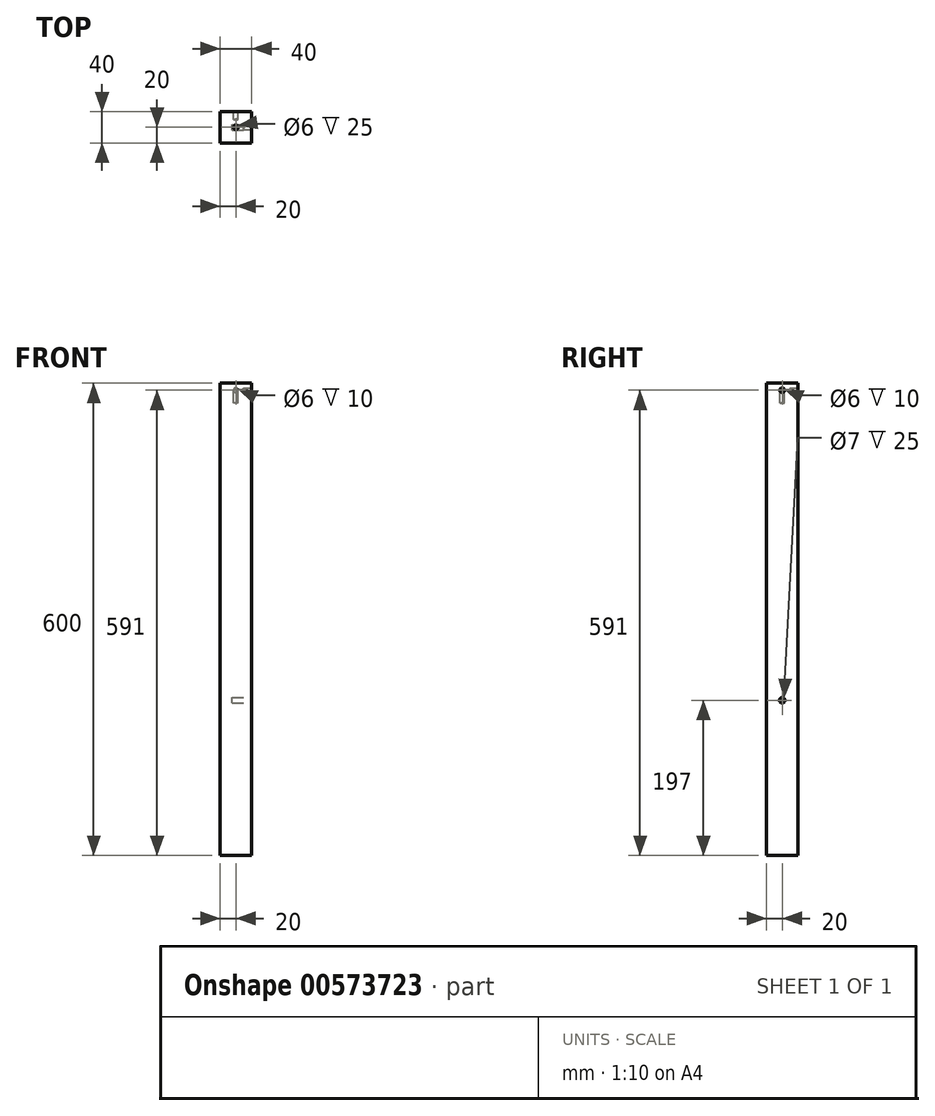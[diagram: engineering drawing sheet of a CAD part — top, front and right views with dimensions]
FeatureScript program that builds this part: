
annotation { "Feature Type Name" : "Feature", "Feature Type Description" : "" }
export const myFeature = defineFeature(function(context is Context, id is Id, definition is map)
    precondition{}
    {
        {
            var Q0;
            Q0=qCreatedBy(makeId("Top.planeOp"),FACE);
            var sketch = newSketch(context, id + "F0", { "sketchPlane" : qUnion([Q0])});
            skLineSegment(sketch, "E0.bottom", {"start": v(0, 0) * mm, "end": v(40, 0) * mm});
            skLineSegment(sketch, "E0.top", {"start": v(0, 40) * mm, "end": v(40, 40) * mm});
            skLineSegment(sketch, "E0.left", {"start": v(0, 0) * mm, "end": v(0, 40) * mm});
            skLineSegment(sketch, "E0.right", {"start": v(40, 0) * mm, "end": v(40, 40) * mm});
            skSolve(sketch);
        }
        {
            var Q0;
            Q0=makeQuery(id+"F0.imprint","IMPRINT",FACE,{"disambiguationData":[TD([[makeQuery(id+"F0.imprint","IMPRINT",EDGE,{"derivedFrom":sQuery(id+"F0.wireOp",EDGE,"E0.bottom")}),1.0]])]});
            extrude(context, id + "F1", {"entities" : qUnion([Q0]), "depth" : 600 * mm, "offsetDistance" : 25 * mm});
        }
        {
            var Q0;
            Q0=makeQuery(id+"F1.opExtrude","CAP_FACE",FACE,{"disambiguationData":[OSD([sQuery(id+"F0.wireOp",EDGE,"E0.bottom"),sQuery(id+"F0.wireOp",EDGE,"E0.top"),sQuery(id+"F0.wireOp",EDGE,"E0.left"),sQuery(id+"F0.wireOp",EDGE,"E0.right")])],"isStart":false});
            var sketch = newSketch(context, id + "F2", { "sketchPlane" : qUnion([Q0])});
            skCircle(sketch, "E1", {"center": v(20, 20) * mm, "radius": 3 * mm});
            skPoint(sketch, "E2", {"position": v(20, 40) * mm});
            skPoint(sketch, "E3", {"position": v(0, 20) * mm});
            skSolve(sketch);
        }
        {
            var Q0;
            Q0 = qSketchRegion(id + "F2", true);
            extrude(context, id + "F3", {"entities" : qUnion([Q0]), "operationType" : NewBodyOperationType.REMOVE, "oppositeDirection" : true, "depth" : 25 * mm, "offsetDistance" : 25 * mm});
        }
        {
            var Q0;
            Q0=makeQuery(id+"F1.opExtrude","SWEPT_FACE",FACE,{"disambiguationData":[OSD([sQuery(id+"F0.wireOp",EDGE,"E0.right")])]});
            var sketch = newSketch(context, id + "F4", { "sketchPlane" : qUnion([Q0])});
            skCircle(sketch, "E4", {"center": v(20, 591) * mm, "radius": 3 * mm});
            skPoint(sketch, "E5", {"position": v(20, 600) * mm});
            skSolve(sketch);
        }
        {
            var Q0;
            Q0 = qSketchRegion(id + "F4", true);
            extrude(context, id + "F5", {"entities" : qUnion([Q0]), "operationType" : NewBodyOperationType.REMOVE, "oppositeDirection" : true, "depth" : 10 * mm, "offsetDistance" : 25 * mm});
        }
        {
            var Q0;
            Q0=makeQuery(id+"F1.opExtrude","SWEPT_FACE",FACE,{"disambiguationData":[OSD([sQuery(id+"F0.wireOp",EDGE,"E0.top")])]});
            var sketch = newSketch(context, id + "F6", { "sketchPlane" : qUnion([Q0])});
            skCircle(sketch, "E6", {"center": v(-20, 591) * mm, "radius": 3 * mm});
            skPoint(sketch, "E7", {"position": v(-20, 600) * mm});
            skSolve(sketch);
        }
        {
            var Q0;
            Q0 = qSketchRegion(id + "F6", true);
            extrude(context, id + "F7", {"entities" : qUnion([Q0]), "operationType" : NewBodyOperationType.REMOVE, "oppositeDirection" : true, "depth" : 10 * mm, "offsetDistance" : 25 * mm});
        }
        {
            var Q0;
            Q0=makeQuery(id+"F1.opExtrude","SWEPT_FACE",FACE,{"disambiguationData":[OSD([sQuery(id+"F0.wireOp",EDGE,"E0.right")])]});
            var sketch = newSketch(context, id + "F8", { "sketchPlane" : qUnion([Q0])});
            skCircle(sketch, "E8", {"center": v(20, 197) * mm, "radius": 3.5 * mm});
            skSolve(sketch);
        }
        {
            var Q0;
            Q0 = qSketchRegion(id + "F8", true);
            extrude(context, id + "F9", {"entities" : qUnion([Q0]), "operationType" : NewBodyOperationType.REMOVE, "oppositeDirection" : true, "depth" : 25 * mm, "offsetDistance" : 25 * mm});
        }
    });
